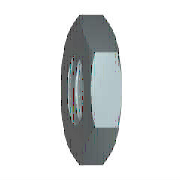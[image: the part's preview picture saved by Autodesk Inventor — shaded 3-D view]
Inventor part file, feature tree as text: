
AUTODESK INVENTOR PART (.ipt)
format: ipt  version: 2019 (Build 230136000, 136)  size: 165,888 bytes
history: native  units: mm (DEFAULTED — no unit token found)
features: sketch x3, chamfer x1, hole x1, other x1, plane x1
ambient origin geometry x7: Origin, YZ Plane, XZ Plane, X Axis, Y Axis, Z Axis, Center Point
bodies: Solid1 (feature_tree), Body (feature_tree)
feature tree (7):
  chamfer  "Chamfer1"  Angle=30.0deg  [1 undecoded]
  hole  "Thread"  [1 undecoded]
  other  "Work Axis1"
  plane  "Work Plane1"
  sketch  "Sketch1"  dims[d0=24.248711mm]
  sketch  "Sketch2"  dims[d1=7.0mm]
  sketch  "Sketch3"  dims[d2=0.0mm d3=30.0deg d4=30.0deg d5=19.64mm d6=19.64mm d7=90.0deg d25=12.376mm d26=6.0mm d27=4.0mm d28=2.0mm d29=14.3117mm d30=8.0mm d31=20.594885mm d8=0.811899mm d9=30.0deg d10=0.811899mm d11=30.0deg d13=0.0mm d14=0.0mm d39=0.0mm d40=0.811899mm d41=0.811899mm d42=0.0mm]
note: 2 required parameter values undecoded (feature->parameter linkage not recoverable at this tier; creation-order binding heuristic only, values carry confidence <= 0.55)
